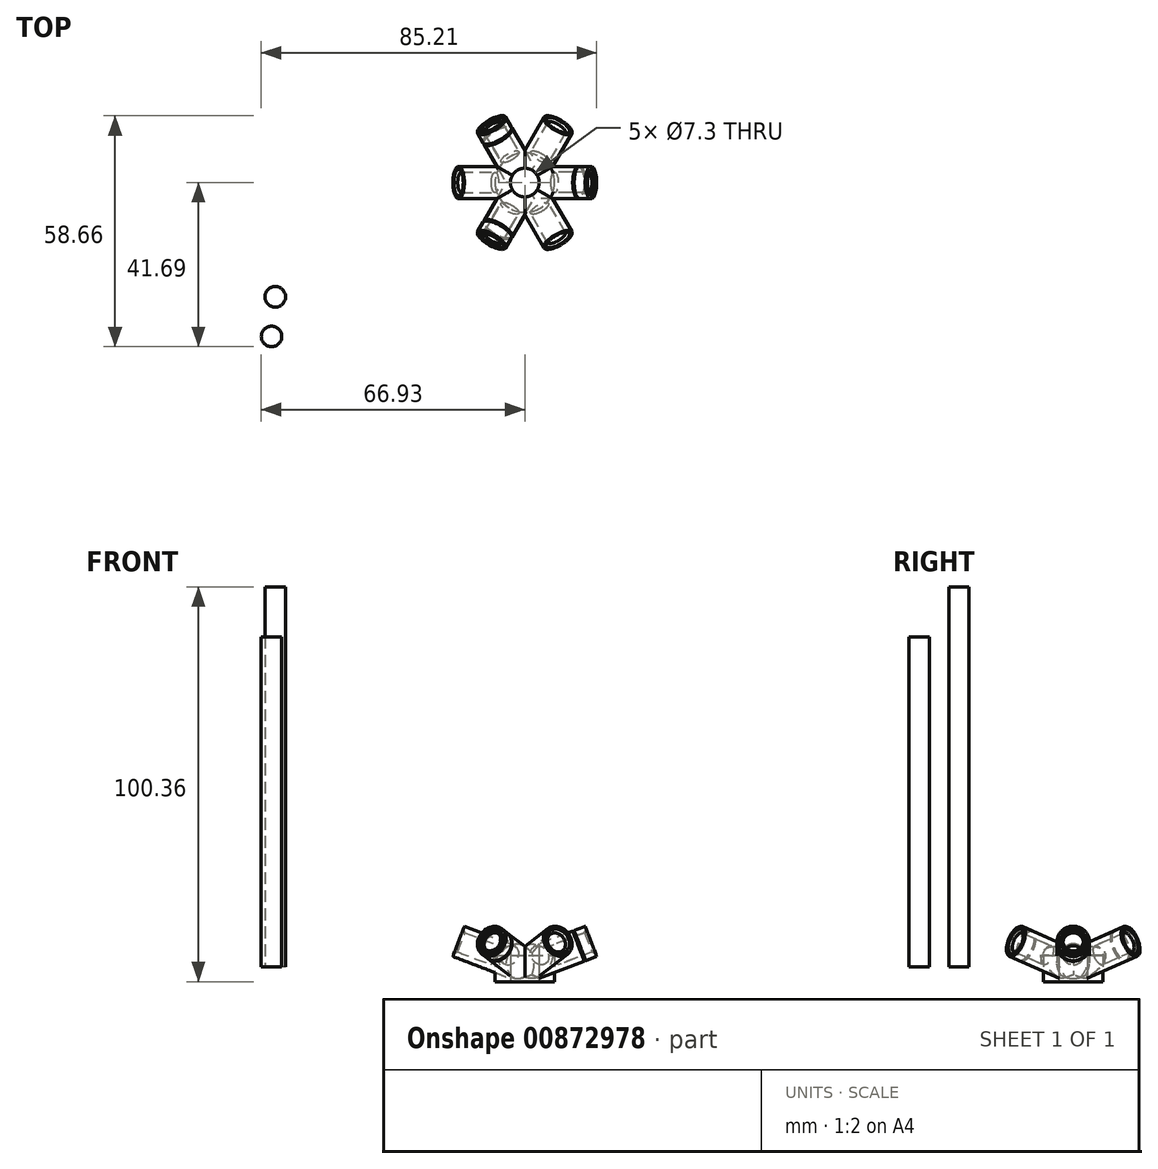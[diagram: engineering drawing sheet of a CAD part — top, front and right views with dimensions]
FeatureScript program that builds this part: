
annotation { "Feature Type Name" : "Feature", "Feature Type Description" : "" }
export const myFeature = defineFeature(function(context is Context, id is Id, definition is map)
    precondition{}
    {
        {
            assignVariable(context, id + "F0", {"name" : "espesor", "anyValue" : 1.5});
        }
        {
            assignVariable(context, id + "F1", {"name" : "longitud", "anyValue" : 18});
        }
        {
            assignVariable(context, id + "F2", {"name" : "relacion", "anyValue" : 1.13});
        }
        {
            assignVariable(context, id + "F3", {"name" : "lvarilla", "anyValue" : 100});
        }
        {
            assignVariable(context, id + "F4", {"name" : "lrecortada", "anyValue" : getVariable(context, 'lvarilla') - 2 * (getVariable(context, 'longitud') * 1.8 / 4)});
        }
        {
            assignVariable(context, id + "F5", {"name" : "lrecortadalarga", "anyValue" : (getVariable(context, 'lvarilla') * getVariable(context, 'relacion') - 2 * (getVariable(context, 'longitud') * 1.8 / 4))});
        }
        {
            var Q0;
            Q0=qCreatedBy(makeId("Front.planeOp"),FACE);
            var sketch = newSketch(context, id + "F6", { "sketchPlane" : qUnion([Q0])});
            skLineSegment(sketch, "E0", {"start": v(0, 0) * mm, "end": v(16.82, 6.42) * mm, "construction": true});
            skLineSegment(sketch, "E1", {"start": v(0, 0) * mm, "end": v(1.46, -3.83) * mm});
            skLineSegment(sketch, "E2", {"start": v(16.82, 6.42) * mm, "end": v(18.28, 2.6) * mm});
            skLineSegment(sketch, "E3", {"start": v(1.46, -3.83) * mm, "end": v(15.1, 1.38) * mm});
            skLineSegment(sketch, "E4", {"start": v(17.74, 4) * mm, "end": v(8.5, 0.46) * mm});
            skLineSegment(sketch, "E5", {"start": v(8.5, 0.46) * mm, "end": v(7.57, 2.9) * mm});
            skLineSegment(sketch, "E6", {"start": v(7.57, 2.9) * mm, "end": v(0, 0) * mm});
            skLineSegment(sketch, "E7", {"start": v(0, 0) * mm, "end": v(0, 41.35) * mm, "construction": true});
            skLineSegment(sketch, "E8", {"start": v(1.46, -3.83) * mm, "end": v(0, -3.83) * mm, "construction": true});
            skLineSegment(sketch, "E9", {"start": v(7.57, 2.9) * mm, "end": v(7.57, -3.83) * mm, "construction": true});
            skLineSegment(sketch, "E10", {"start": v(7.57, -3.83) * mm, "end": v(1.46, -3.83) * mm, "construction": true});
            skLineSegment(sketch, "E11", {"start": v(0, -3.83) * mm, "end": v(7.57, -3.83) * mm});
            skLineSegment(sketch, "E12", {"start": v(7.57, -3.83) * mm, "end": v(7.57, 2.9) * mm});
            skLineSegment(sketch, "E13", {"start": v(0, 2.9) * mm, "end": v(7.57, 2.9) * mm});
            skLineSegment(sketch, "E14", {"start": v(0, 2.9) * mm, "end": v(0, -3.83) * mm});
            skLineSegment(sketch, "E15", {"start": v(15.48, 1.52) * mm, "end": v(15.44, 1.62) * mm});
            skLineSegment(sketch, "E16", {"start": v(15.44, 1.62) * mm, "end": v(15.07, 1.47) * mm});
            skLineSegment(sketch, "E17", {"start": v(15.07, 1.47) * mm, "end": v(15.1, 1.38) * mm});
            skLineSegment(sketch, "E18.trimOffspring", {"start": v(15.48, 1.52) * mm, "end": v(18.28, 2.6) * mm});
            skSolve(sketch);
        }
        {
            var Q0;
            Q0=qCreatedBy(makeId("Front.planeOp"),FACE);
            var sketch = newSketch(context, id + "F7", { "sketchPlane" : qUnion([Q0])});
            skLineSegment(sketch, "E19", {"start": v(0, 0) * mm, "end": v(0, 45.08) * mm, "construction": true});
            skLineSegment(sketch, "E20.MirrorCS", {"start": v(-8.5, 0.46) * mm, "end": v(-7.57, 2.9) * mm});
            skLineSegment(sketch, "E21.MirrorCS", {"start": v(-16.82, 6.42) * mm, "end": v(-18.28, 2.6) * mm});
            skLineSegment(sketch, "E22.MirrorCS", {"start": v(-7.57, 2.9) * mm, "end": v(0, 0) * mm});
            skLineSegment(sketch, "E23.MirrorCS", {"start": v(0, 0) * mm, "end": v(-16.82, 6.42) * mm, "construction": true});
            skLineSegment(sketch, "E24.MirrorCS", {"start": v(0, 2.9) * mm, "end": v(-7.57, 2.9) * mm});
            skLineSegment(sketch, "E25.MirrorCS", {"start": v(-17.74, 4) * mm, "end": v(-8.5, 0.46) * mm});
            skLineSegment(sketch, "E26", {"start": v(-18.28, 2.6) * mm, "end": v(-1.46, -3.83) * mm});
            skLineSegment(sketch, "E27", {"start": v(0, 0) * mm, "end": v(-1.46, -3.83) * mm});
            skLineSegment(sketch, "E28", {"start": v(-1.46, -3.83) * mm, "end": v(-7.57, -3.83) * mm});
            skLineSegment(sketch, "E29", {"start": v(-1.46, -3.83) * mm, "end": v(0, -3.83) * mm});
            skLineSegment(sketch, "E30", {"start": v(0, -3.83) * mm, "end": v(0, 2.9) * mm});
            skLineSegment(sketch, "E31", {"start": v(-7.57, 2.9) * mm, "end": v(-7.57, -3.83) * mm});
            skSolve(sketch);
        }
        {
            var Q0;
            {var subQ1=sQuery(id+"F6.wireOp",EDGE,"E4");Q0=makeQuery(id+"F6.imprint","IMPRINT",FACE,{"disambiguationData":[TD([[makeQuery(id+"F6.imprint","IMPRINT",EDGE,{"derivedFrom":subQ1}),1.0]])]});}
            var Q1;
            {var subQ0=sQuery(id+"F6.wireOp",EDGE,"E1");Q1=makeQuery(id+"F6.imprint","IMPRINT",FACE,{"disambiguationData":[TD([[makeQuery(id+"F6.imprint","IMPRINT",EDGE,{"derivedFrom":subQ0}),1.0]])]});}
            var Q2;
            Q2=sQuery(id+"F6.wireOp",EDGE,"E0");
            revolve(context, id + "F8", {"surfaceOperationType" : NewSurfaceOperationType.NEW, "entities" : qUnion([Q0, Q1]), "axis" : qUnion([Q2]), "revolveType" : RevolveType.FULL});
        }
        {
            var Q0;
            {var subQ5=sQuery(id+"F7.wireOp",EDGE,"E20.MirrorCS");Q0=makeQuery(id+"F7.imprint","IMPRINT",FACE,{"disambiguationData":[TD([[makeQuery(id+"F7.imprint","IMPRINT",EDGE,{"derivedFrom":subQ5}),-1.0]])]});}
            var Q1;
            {var subQ0=sQuery(id+"F7.wireOp",EDGE,"E22.MirrorCS");Q1=makeQuery(id+"F7.imprint","IMPRINT",FACE,{"disambiguationData":[TD([[makeQuery(id+"F7.imprint","IMPRINT",EDGE,{"derivedFrom":subQ0}),-1.0]])]});}
            var Q2;
            Q2=sQuery(id+"F7.wireOp",EDGE,"E23.MirrorCS");
            revolve(context, id + "F9", {"surfaceOperationType" : NewSurfaceOperationType.NEW, "entities" : qUnion([Q0, Q1]), "axis" : qUnion([Q2]), "revolveType" : RevolveType.FULL});
        }
        {
            var Q0;
            Q0=makeQuery(id+"F8.opRevolve","SWEPT_BODY",BODY,{"disambiguationData":[OSD([sQuery(id+"F6.wireOp",EDGE,"E1"),sQuery(id+"F6.wireOp",EDGE,"E2"),sQuery(id+"F6.wireOp",EDGE,"E3"),sQuery(id+"F6.wireOp",EDGE,"E4"),sQuery(id+"F6.wireOp",EDGE,"E5"),sQuery(id+"F6.wireOp",EDGE,"E6")])]});
            var Q1;
            Q1=sQuery(id+"F6.wireOp",EDGE,"E7");
            circularPattern(context, id + "F10", {"operationType" : NewBodyOperationType.ADD, "entities" : qUnion([Q0]), "axis" : qUnion([Q1]), "angle" : 360 * degree, "instanceCount" : 3, "equalSpace" : true});
        }
        {
            var Q0;
            Q0=makeQuery(id+"FgpRCOrkwi8NXZ9_2.boolean.opBoolean","SPLIT",BODY,{"disambiguationData":[OD(1.0)],"derivedFrom":makeQuery(id+"F9.opRevolve","SWEPT_BODY",BODY,{"disambiguationData":[OSD([sQuery(id+"F7.wireOp",EDGE,"E20.MirrorCS"),sQuery(id+"F7.wireOp",EDGE,"E21.MirrorCS"),sQuery(id+"F7.wireOp",EDGE,"E22.MirrorCS"),sQuery(id+"F7.wireOp",EDGE,"E25.MirrorCS"),sQuery(id+"F7.wireOp",EDGE,"E26"),sQuery(id+"F7.wireOp",EDGE,"E27")])]})});
            var Q1;
            Q1=sQuery(id+"F7.wireOp",EDGE,"E19");
            circularPattern(context, id + "F11", {"entities" : qUnion([Q0]), "axis" : qUnion([Q1]), "angle" : 360 * degree, "instanceCount" : 3, "equalSpace" : true});
        }
        {
            var Q0;
            {var subQ0=sQuery(id+"F6.wireOp",EDGE,"E1");Q0=makeQuery(id+"F6.imprint","IMPRINT",FACE,{"disambiguationData":[TD([[makeQuery(id+"F6.imprint","IMPRINT",EDGE,{"derivedFrom":subQ0}),-1.0]])]});}
            var Q1;
            {var subQ0=sQuery(id+"F6.wireOp",EDGE,"E1");Q1=makeQuery(id+"F6.imprint","IMPRINT",FACE,{"disambiguationData":[TD([[makeQuery(id+"F6.imprint","IMPRINT",EDGE,{"derivedFrom":subQ0}),1.0]])]});}
            var Q2;
            {var subQ0=sQuery(id+"F6.wireOp",EDGE,"E11");var subQ3=sQuery(id+"F6.wireOp",EDGE,"E12");var subQ5=makeQuery(id+"F6.imprint","INTERSECT",VERTEX,{"derivedFrom":[subQ0,subQ3]});Q2=makeQuery(id+"F6.imprint","IMPRINT",FACE,{"disambiguationData":[TD([[makeQuery(id+"F6.imprint","IMPRINT",EDGE,{"disambiguationData":[TD([[subQ5,-1.0]])],"derivedFrom":subQ3}),1.0]])]});}
            var Q3;
            {var subQ0=sQuery(id+"F6.wireOp",EDGE,"E6");Q3=makeQuery(id+"F6.imprint","IMPRINT",FACE,{"disambiguationData":[TD([[makeQuery(id+"F6.imprint","IMPRINT",EDGE,{"derivedFrom":subQ0}),-1.0]])]});}
            var Q4;
            Q4=sQuery(id+"F6.wireOp",EDGE,"E13");
            var Q5;
            Q5=sQuery(id+"F6.wireOp",EDGE,"E14");
            var Q6;
            Q6=sQuery(id+"F6.wireOp",EDGE,"E7");
            revolve(context, id + "F12", {"surfaceOperationType" : NewSurfaceOperationType.NEW, "entities" : qUnion([Q0, Q1, Q2, Q3]), "surfaceEntities" : qUnion([Q4, Q5]), "axis" : qUnion([Q6]), "revolveType" : RevolveType.FULL});
        }
        {
            var Q0;
            {var subQ0=sQuery(id+"F7.wireOp",EDGE,"E22.MirrorCS");Q0=makeQuery(id+"F7.imprint","IMPRINT",FACE,{"disambiguationData":[TD([[makeQuery(id+"F7.imprint","IMPRINT",EDGE,{"derivedFrom":subQ0}),1.0]])]});}
            var Q1;
            {var subQ0=sQuery(id+"F7.wireOp",EDGE,"E22.MirrorCS");Q1=makeQuery(id+"F7.imprint","IMPRINT",FACE,{"disambiguationData":[TD([[makeQuery(id+"F7.imprint","IMPRINT",EDGE,{"derivedFrom":subQ0}),-1.0]])]});}
            var Q2;
            {var subQ0=sQuery(id+"F7.wireOp",EDGE,"E27");Q2=makeQuery(id+"F7.imprint","IMPRINT",FACE,{"disambiguationData":[TD([[makeQuery(id+"F7.imprint","IMPRINT",EDGE,{"derivedFrom":subQ0}),1.0]])]});}
            var Q3;
            {var subQ0=sQuery(id+"F7.wireOp",EDGE,"E28");Q3=makeQuery(id+"F7.imprint","IMPRINT",FACE,{"disambiguationData":[TD([[makeQuery(id+"F7.imprint","IMPRINT",EDGE,{"derivedFrom":subQ0}),-1.0]])]});}
            var Q4;
            Q4=sQuery(id+"F7.wireOp",EDGE,"E19");
            revolve(context, id + "F13", {"surfaceOperationType" : NewSurfaceOperationType.NEW, "entities" : qUnion([Q0, Q1, Q2, Q3]), "axis" : qUnion([Q4]), "revolveType" : RevolveType.FULL});
        }
        {
            var Q0;
            Q0=makeQuery(id+"F10.opPattern","COPY",EDGE,{"derivedFrom":makeQuery(id+"F8.opRevolve","SWEPT_EDGE",EDGE,{"disambiguationData":[OSD([sQuery(id+"F6.wireOp",EDGE,"E2"),sQuery(id+"F6.wireOp",EDGE,"E4")])]}),"instanceName":"5"});
            var Q1;
            Q1=makeQuery(id+"F10.opPattern","COPY",EDGE,{"derivedFrom":makeQuery(id+"F8.opRevolve","SWEPT_EDGE",EDGE,{"disambiguationData":[OSD([sQuery(id+"F6.wireOp",EDGE,"E2"),sQuery(id+"F6.wireOp",EDGE,"E4")])]}),"instanceName":"4"});
            var Q2;
            Q2=makeQuery(id+"F8.opRevolve","SWEPT_EDGE",EDGE,{"disambiguationData":[OSD([sQuery(id+"F6.wireOp",EDGE,"E2"),sQuery(id+"F6.wireOp",EDGE,"E4")])]});
            var Q3;
            Q3=makeQuery(id+"F10.opPattern","COPY",EDGE,{"derivedFrom":makeQuery(id+"F8.opRevolve","SWEPT_EDGE",EDGE,{"disambiguationData":[OSD([sQuery(id+"F6.wireOp",EDGE,"E2"),sQuery(id+"F6.wireOp",EDGE,"E4")])]}),"instanceName":"1"});
            var Q4;
            Q4=makeQuery(id+"F10.opPattern","COPY",EDGE,{"derivedFrom":makeQuery(id+"F8.opRevolve","SWEPT_EDGE",EDGE,{"disambiguationData":[OSD([sQuery(id+"F6.wireOp",EDGE,"E2"),sQuery(id+"F6.wireOp",EDGE,"E4")])]}),"instanceName":"2"});
            var Q5;
            Q5=makeQuery(id+"F10.opPattern","COPY",EDGE,{"derivedFrom":makeQuery(id+"F8.opRevolve","SWEPT_EDGE",EDGE,{"disambiguationData":[OSD([sQuery(id+"F6.wireOp",EDGE,"E2"),sQuery(id+"F6.wireOp",EDGE,"E4")])]}),"instanceName":"3"});
            var Q6;
            Q6=makeQuery(id+"F11.opPattern","COPY",EDGE,{"derivedFrom":makeQuery(id+"F9.opRevolve","SWEPT_EDGE",EDGE,{"disambiguationData":[OSD([sQuery(id+"F7.wireOp",EDGE,"E21.MirrorCS"),sQuery(id+"F7.wireOp",EDGE,"E25.MirrorCS")])]}),"instanceName":"2"});
            var Q7;
            Q7=makeQuery(id+"F9.opRevolve","SWEPT_EDGE",EDGE,{"disambiguationData":[OSD([sQuery(id+"F7.wireOp",EDGE,"E21.MirrorCS"),sQuery(id+"F7.wireOp",EDGE,"E25.MirrorCS")])]});
            var Q8;
            Q8=makeQuery(id+"F11.opPattern","COPY",EDGE,{"derivedFrom":makeQuery(id+"F9.opRevolve","SWEPT_EDGE",EDGE,{"disambiguationData":[OSD([sQuery(id+"F7.wireOp",EDGE,"E21.MirrorCS"),sQuery(id+"F7.wireOp",EDGE,"E25.MirrorCS")])]}),"instanceName":"1"});
            chamfer(context, id + "F14", {"entities" : qUnion([Q0, Q1, Q2, Q3, Q4, Q5, Q6, Q7, Q8]), "width" : (getVariable(context, 'espesor') / 2) * mm, "tangentPropagation" : true});
        }
        {
            var Q0;
            Q0=qCreatedBy(makeId("Top.planeOp"),FACE);
            var sketch = newSketch(context, id + "F15", { "sketchPlane" : qUnion([Q0])});
            skCircle(sketch, "E32", {"center": v(-64.33, -39.09) * mm, "radius": 2.6 * mm});
            skCircle(sketch, "E33", {"center": v(-63.38, -29.03) * mm, "radius": 2.6 * mm});
            skSolve(sketch);
        }
        {
            var Q0;
            Q0=makeQuery(id+"F15.imprint","IMPRINT",FACE,{"disambiguationData":[TD([[makeQuery(id+"F15.imprint","IMPRINT",EDGE,{"derivedFrom":sQuery(id+"F15.wireOp",EDGE,"E32")}),1.0]])]});
            extrude(context, id + "F16", {"entities" : qUnion([Q0]), "depth" : (getVariable(context, 'lrecortada')) * mm, "offsetDistance" : 25 * mm});
        }
        {
            var Q0;
            Q0=makeQuery(id+"F15.imprint","IMPRINT",FACE,{"disambiguationData":[TD([[makeQuery(id+"F15.imprint","IMPRINT",EDGE,{"derivedFrom":sQuery(id+"F15.wireOp",EDGE,"E33")}),1.0]])]});
            extrude(context, id + "F17", {"entities" : qUnion([Q0]), "depth" : (getVariable(context, 'lrecortadalarga')) * mm, "offsetDistance" : 25 * mm});
        }
        {
            var Q0;
            Q0=qCreatedBy(makeId("Top.planeOp"),FACE);
            var sketch = newSketch(context, id + "F18", { "sketchPlane" : qUnion([Q0])});
            skCircle(sketch, "E34", {"center": v(0, 0) * mm, "radius": 3.65 * mm});
            skSolve(sketch);
        }
        {
            var Q0;
            Q0=qSketchRegion(id+"F18",true);
            extrude(context, id + "F19", {"entities" : qUnion([Q0]), "operationType" : NewBodyOperationType.REMOVE, "depth" : 200 * mm, "offsetDistance" : 25 * mm, "symmetric" : true});
        }
    });
